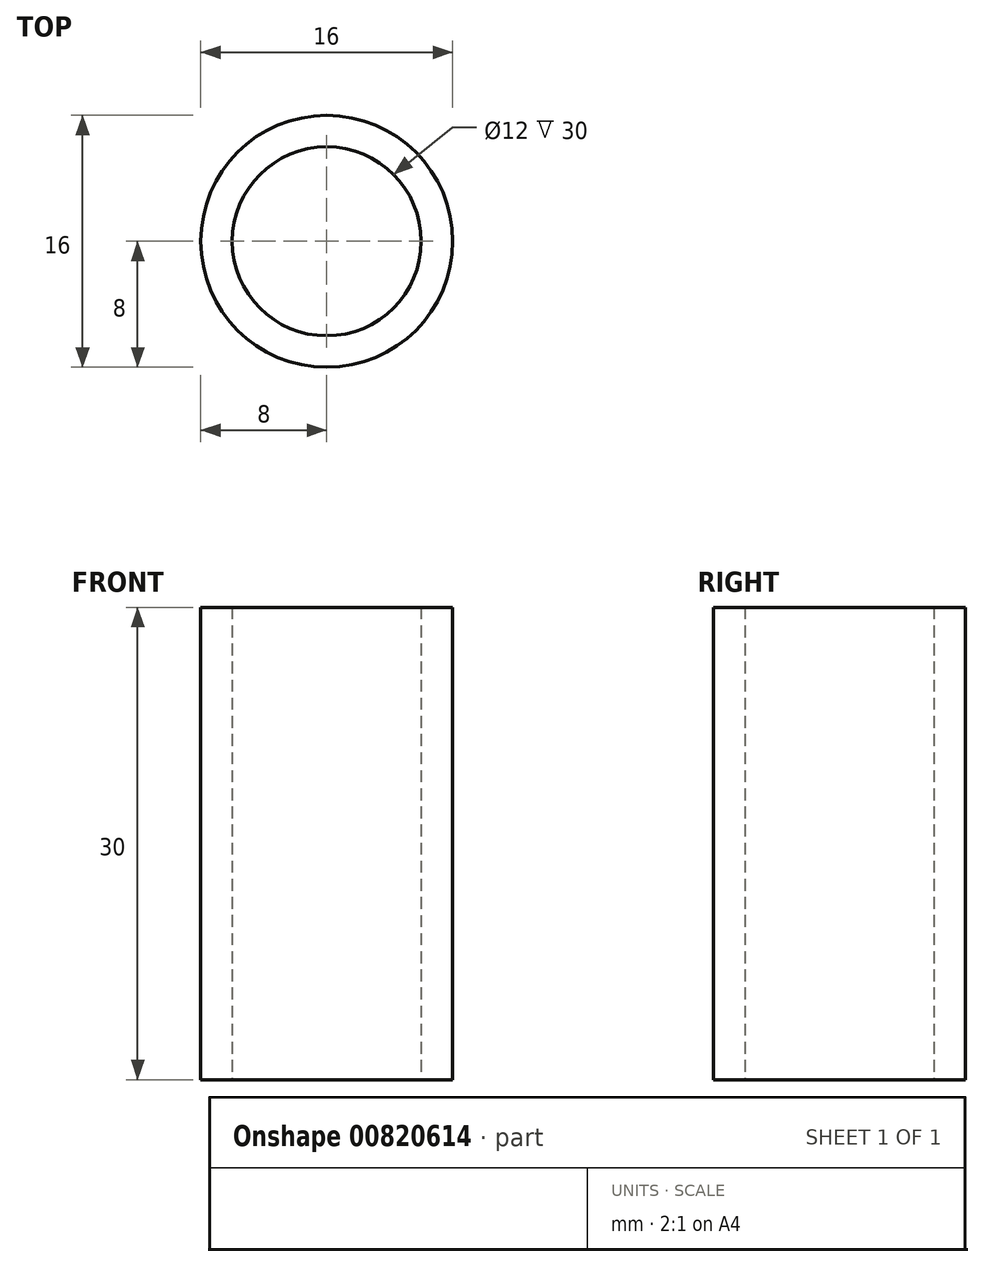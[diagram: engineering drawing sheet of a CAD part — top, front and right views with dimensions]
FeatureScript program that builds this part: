
annotation { "Feature Type Name" : "Feature", "Feature Type Description" : "" }
export const myFeature = defineFeature(function(context is Context, id is Id, definition is map)
    precondition{}
    {
        {
            var Q0;
            Q0=qCreatedBy(makeId("Top.planeOp"),FACE);
            var sketch = newSketch(context, id + "F0", { "sketchPlane" : qUnion([Q0])});
            skCircle(sketch, "E0", {"center": v(0, 0) * mm, "radius": 6 * mm});
            skCircle(sketch, "E1", {"center": v(0, 0) * mm, "radius": 8 * mm});
            skSolve(sketch);
        }
        {
            var Q0;
            Q0=makeQuery(id+"F0.imprint","IMPRINT",FACE,{"disambiguationData":[TD([[makeQuery(id+"F0.imprint","IMPRINT",EDGE,{"derivedFrom":sQuery(id+"F0.wireOp",EDGE,"E0")}),-1.0]])]});
            var Q1;
            Q1=makeQuery(id+"F0.imprint","IMPRINT",FACE,{"disambiguationData":[TD([[makeQuery(id+"F0.imprint","IMPRINT",EDGE,{"derivedFrom":sQuery(id+"F0.wireOp",EDGE,"612fde89-3595-444e-9fb7-2ffa0ac8abad.1.0.0")}),1.0]])]});
            var Q2;
            Q2=makeQuery(id+"F0.imprint","IMPRINT",FACE,{"disambiguationData":[TD([[makeQuery(id+"F0.imprint","IMPRINT",EDGE,{"derivedFrom":sQuery(id+"F0.wireOp",EDGE,"612fde89-3595-444e-9fb7-2ffa0ac8abad.2.0.0")}),1.0]])]});
            var Q3;
            Q3=makeQuery(id+"F0.imprint","IMPRINT",FACE,{"disambiguationData":[TD([[makeQuery(id+"F0.imprint","IMPRINT",EDGE,{"derivedFrom":sQuery(id+"F0.wireOp",EDGE,"edc787e6-a8b2-48df-92bf-5eb6b0130844.0.3.0")}),1.0]])]});
            var Q4;
            Q4=makeQuery(id+"F0.imprint","IMPRINT",FACE,{"disambiguationData":[TD([[makeQuery(id+"F0.imprint","IMPRINT",EDGE,{"derivedFrom":sQuery(id+"F0.wireOp",EDGE,"edc787e6-a8b2-48df-92bf-5eb6b0130844.0.3.1")}),1.0]])]});
            var Q5;
            Q5=makeQuery(id+"F0.imprint","IMPRINT",FACE,{"disambiguationData":[TD([[makeQuery(id+"F0.imprint","IMPRINT",EDGE,{"derivedFrom":sQuery(id+"F0.wireOp",EDGE,"612fde89-3595-444e-9fb7-2ffa0ac8abad.2.1.0")}),1.0]])]});
            var Q6;
            Q6=makeQuery(id+"F0.imprint","IMPRINT",FACE,{"disambiguationData":[TD([[makeQuery(id+"F0.imprint","IMPRINT",EDGE,{"derivedFrom":sQuery(id+"F0.wireOp",EDGE,"612fde89-3595-444e-9fb7-2ffa0ac8abad.1.1.0")}),1.0]])]});
            var Q7;
            Q7=makeQuery(id+"F0.imprint","IMPRINT",FACE,{"disambiguationData":[TD([[makeQuery(id+"F0.imprint","IMPRINT",EDGE,{"derivedFrom":sQuery(id+"F0.wireOp",EDGE,"612fde89-3595-444e-9fb7-2ffa0ac8abad.0.1.0")}),1.0]])]});
            var Q8;
            Q8=makeQuery(id+"F0.imprint","IMPRINT",FACE,{"disambiguationData":[TD([[makeQuery(id+"F0.imprint","IMPRINT",EDGE,{"derivedFrom":sQuery(id+"F0.wireOp",EDGE,"b4ad77dd-359b-4d26-a60d-15efb589b3f4.0.0.2")}),1.0]])]});
            var Q9;
            Q9=makeQuery(id+"F0.imprint","IMPRINT",FACE,{"disambiguationData":[TD([[makeQuery(id+"F0.imprint","IMPRINT",EDGE,{"derivedFrom":sQuery(id+"F0.wireOp",EDGE,"b4ad77dd-359b-4d26-a60d-15efb589b3f4.0.1.2")}),1.0]])]});
            var Q10;
            Q10=makeQuery(id+"F0.imprint","IMPRINT",FACE,{"disambiguationData":[TD([[makeQuery(id+"F0.imprint","IMPRINT",EDGE,{"derivedFrom":sQuery(id+"F0.wireOp",EDGE,"b4ad77dd-359b-4d26-a60d-15efb589b3f4.0.2.2")}),1.0]])]});
            var Q11;
            Q11=makeQuery(id+"F0.imprint","IMPRINT",FACE,{"disambiguationData":[TD([[makeQuery(id+"F0.imprint","IMPRINT",EDGE,{"derivedFrom":sQuery(id+"F0.wireOp",EDGE,"b4ad77dd-359b-4d26-a60d-15efb589b3f4.0.3.2")}),1.0]])]});
            extrude(context, id + "F1", {"entities" : qUnion([Q0, Q1, Q2, Q3, Q4, Q5, Q6, Q7, Q8, Q9, Q10, Q11]), "depth" : 30 * mm, "offsetDistance" : 25 * mm});
        }
    });
